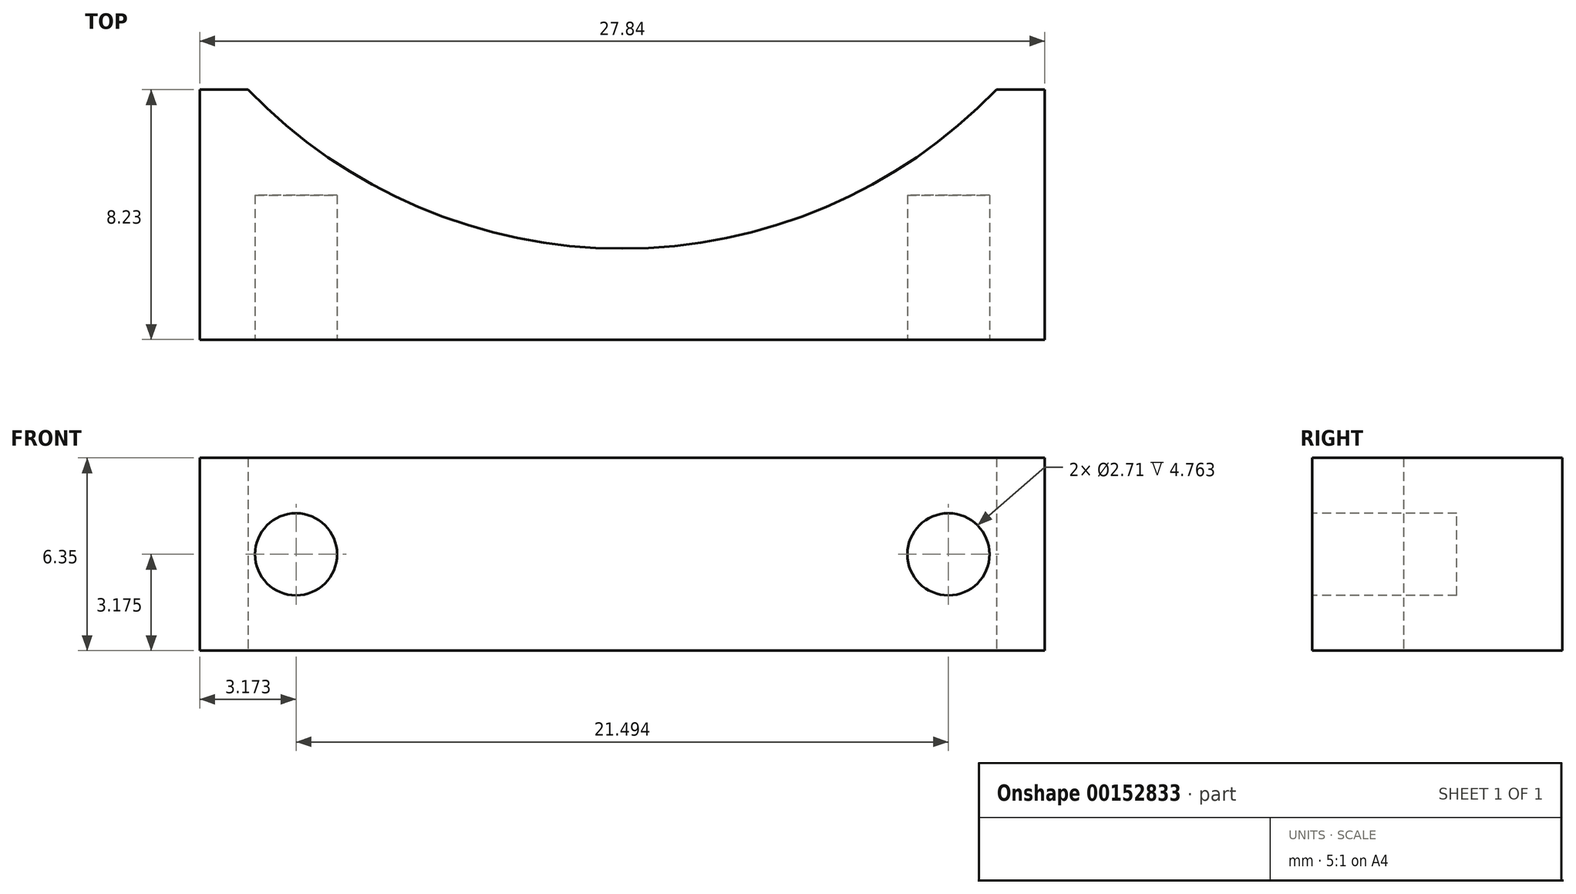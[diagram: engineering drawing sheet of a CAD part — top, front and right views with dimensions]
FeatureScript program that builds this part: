
annotation { "Feature Type Name" : "Feature", "Feature Type Description" : "" }
export const myFeature = defineFeature(function(context is Context, id is Id, definition is map)
    precondition{}
    {
        {
            var Q0;
            Q0=qCreatedBy(makeId("Top.planeOp"),FACE);
            var sketch = newSketch(context, id + "F0", { "sketchPlane" : qUnion([Q0])});
            skArc(sketch, "E0", {"start": v(-12.33, -11.9) * mm, "mid": v(0, -17.15) * mm, "end": v(12.33, -11.9) * mm});
            skLineSegment(sketch, "E1", {"start": v(-13.92, -11.9) * mm, "end": v(-12.33, -11.9) * mm});
            skLineSegment(sketch, "E2", {"start": v(12.33, -11.9) * mm, "end": v(13.92, -11.9) * mm});
            skLineSegment(sketch, "E3", {"start": v(-13.92, -11.9) * mm, "end": v(-13.92, -20.14) * mm});
            skLineSegment(sketch, "E4", {"start": v(-13.92, -20.14) * mm, "end": v(13.92, -20.14) * mm});
            skLineSegment(sketch, "E5", {"start": v(13.92, -20.14) * mm, "end": v(13.92, -11.9) * mm});
            skLineSegment(sketch, "E6", {"start": v(10.75, -20.14) * mm, "end": v(10.75, -15.38) * mm, "construction": true});
            skLineSegment(sketch, "E7", {"start": v(8.92, -15.38) * mm, "end": v(12.58, -15.38) * mm, "construction": true});
            skLineSegment(sketch, "E8", {"start": v(0, -20.14) * mm, "end": v(0, 0) * mm, "construction": true});
            skLineSegment(sketch, "E9", {"start": v(8.92, -15.38) * mm, "end": v(7.57, -15.38) * mm, "construction": true});
            skLineSegment(sketch, "E10", {"start": v(12.58, -15.38) * mm, "end": v(13.92, -15.38) * mm, "construction": true});
            skSolve(sketch);
        }
        {
            var Q0;
            Q0 = qSketchRegion(id + "F0", true);
            extrude(context, id + "F1", {"entities" : qUnion([Q0]), "depth" : 6.35 * mm});
        }
        {
            var Q0;
            Q0=makeQuery(id+"F1.opExtrude","SWEPT_FACE",FACE,{"disambiguationData":[OSD([sQuery(id+"F0.wireOp",EDGE,"E4")])]});
            var sketch = newSketch(context, id + "F2", { "sketchPlane" : qUnion([Q0])});
            skLineSegment(sketch, "E11", {"start": v(-13.92, 3.18) * mm, "end": v(-10.75, 3.18) * mm, "construction": true});
            skLineSegment(sketch, "E12", {"start": v(-10.75, 3.18) * mm, "end": v(-10.75, 0) * mm, "construction": true});
            skLineSegment(sketch, "E13", {"start": v(13.92, 3.18) * mm, "end": v(10.75, 3.18) * mm, "construction": true});
            skCircle(sketch, "E14", {"center": v(-10.75, 3.18) * mm, "radius": 1.35 * mm});
            skCircle(sketch, "E15", {"center": v(10.75, 3.18) * mm, "radius": 1.35 * mm});
            skSolve(sketch);
        }
        {
            var Q0;
            Q0 = qSketchRegion(id + "F2", true);
            extrude(context, id + "F3", {"entities" : qUnion([Q0]), "operationType" : NewBodyOperationType.REMOVE, "oppositeDirection" : true, "depth" : 4.76 * mm});
        }
    });
